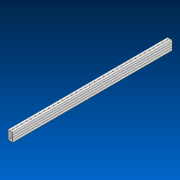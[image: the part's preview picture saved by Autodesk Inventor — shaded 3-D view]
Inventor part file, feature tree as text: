
AUTODESK INVENTOR PART (.ipt)
format: ipt  version: 2022.2 (Build 262287000, 287)  size: 529,920 bytes
history: native  units: in
note: dims shown in document units (in); Inventor stores cm internally (conversion verified against a paired STEP export)
features: other x36, extrude x1, pattern_linear x1, sketch x1
ambient origin geometry x8: Origin, YZ Plane, XZ Plane, XY Plane, X Axis, Y Axis, Z Axis, Center Point
bodies: Solid1 (feature_tree)
feature tree (39):
  extrude  "Extrusion1"  Depth=2.0in
  other  "Work Axis1"
  pattern_linear  "Rectangular Pattern1"  Spacing1=24.0in  [1 undecoded]
  sketch  "Sketch1"  dims[d0=1.0in d1=2.0in d2=24.0in d3=0.0in d4=13.7795in d6=1.0in]
  other  "Work Axis2"
  other  "Work Axis3"
  other  "Work Axis4"
  other  "Work Axis5"
  other  "Work Axis6"
  other  "Work Axis7"
  other  "Work Axis8"
  other  "Work Axis9"
  other  "Work Axis10"
  other  "Work Axis60"
  other  "Work Axis61"
  other  "Work Axis62"
  other  "Work Axis63"
  other  "Work Axis64"
  other  "Work Axis65"
  other  "Work Axis66"
  other  "Work Axis67"
  other  "Work Axis68"
  other  "Work Axis69"
  other  "Work Axis70"
  other  "Work Axis71"
  other  "Work Axis72"
  other  "Work Axis73"
  other  "Work Axis74"
  other  "Work Axis75"
  other  "Work Axis76"
  other  "Work Axis77"
  other  "Work Axis78"
  other  "Work Axis79"
  other  "Work Axis80"
  other  "Work Axis81"
  other  "Work Axis82"
  other  "Work Axis83"
  other  "Work Axis84"
  other  "Cut-Extrude2"
note: 1 required parameter value undecoded (feature->parameter linkage not recoverable at this tier; creation-order binding heuristic only, values carry confidence <= 0.55)
